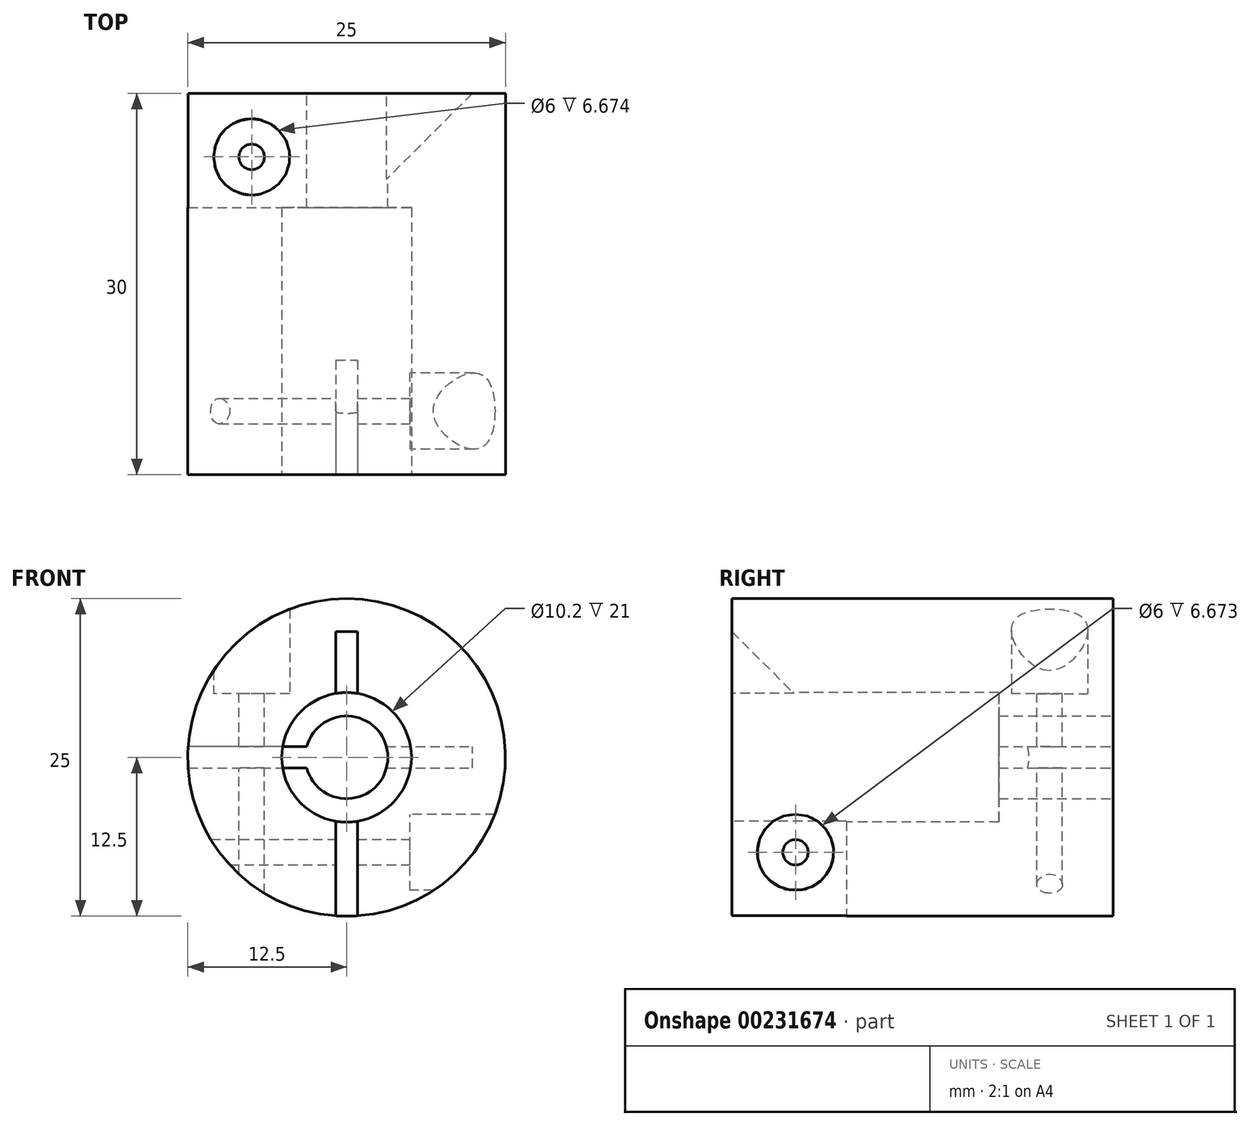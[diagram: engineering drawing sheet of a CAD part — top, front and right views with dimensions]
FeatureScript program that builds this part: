
annotation { "Feature Type Name" : "Feature", "Feature Type Description" : "" }
export const myFeature = defineFeature(function(context is Context, id is Id, definition is map)
    precondition{}
    {
        {
            var Q0;
            Q0=qCreatedBy(makeId("Front.planeOp"),FACE);
            var sketch = newSketch(context, id + "F0", { "sketchPlane" : qUnion([Q0])});
            skCircle(sketch, "E0", {"center": v(0, 0) * mm, "radius": 12.5 * mm});
            skSolve(sketch);
        }
        {
            var Q0;
            Q0 = qSketchRegion(id + "F0", true);
            extrude(context, id + "F1", {"entities" : qUnion([Q0]), "oppositeDirection" : true, "depth" : 30 * mm});
        }
        {
            var Q0;
            Q0=makeQuery(id+"F1.opExtrude","CAP_FACE",FACE,{"disambiguationData":[OSD([sQuery(id+"F0.wireOp",EDGE,"E0")])],"isStart":true});
            var sketch = newSketch(context, id + "F2", { "sketchPlane" : qUnion([Q0])});
            skCircle(sketch, "E1", {"center": v(0, 0) * mm, "radius": 5.1 * mm});
            skSolve(sketch);
        }
        {
            var Q0;
            Q0 = qSketchRegion(id + "F2", true);
            extrude(context, id + "F3", {"entities" : qUnion([Q0]), "operationType" : NewBodyOperationType.REMOVE, "oppositeDirection" : true, "depth" : 21 * mm});
        }
        {
            var Q0;
            Q0=makeQuery(id+"F1.opExtrude","CAP_FACE",FACE,{"disambiguationData":[OSD([sQuery(id+"F0.wireOp",EDGE,"E0")])],"isStart":false});
            var sketch = newSketch(context, id + "F4", { "sketchPlane" : qUnion([Q0])});
            skCircle(sketch, "E2", {"center": v(0, 0) * mm, "radius": 3.25 * mm});
            skSolve(sketch);
        }
        {
            var Q0;
            Q0 = qSketchRegion(id + "F4", true);
            extrude(context, id + "F5", {"entities" : qUnion([Q0]), "operationType" : NewBodyOperationType.REMOVE, "oppositeDirection" : true, "depth" : 30 * mm});
        }
        {
            var Q0;
            Q0=makeQuery(id+"F1.opExtrude","CAP_FACE",FACE,{"disambiguationData":[OSD([sQuery(id+"F0.wireOp",EDGE,"E0")])],"isStart":false});
            var sketch = newSketch(context, id + "F6", { "sketchPlane" : qUnion([Q0])});
            skLineSegment(sketch, "E3", {"start": v(3.14, 0.85) * mm, "end": v(12.47, 0.85) * mm});
            skLineSegment(sketch, "E4", {"start": v(12.47, -0.85) * mm, "end": v(3.14, -0.85) * mm});
            skArc(sketch, "E5", {"start": v(3.14, -0.85) * mm, "mid": v(3.25, 0) * mm, "end": v(3.14, 0.85) * mm});
            skArc(sketch, "E6", {"start": v(12.47, -0.85) * mm, "mid": v(12.5, 0) * mm, "end": v(12.47, 0.85) * mm});
            skLineSegment(sketch, "E7", {"start": v(0, 0) * mm, "end": v(12.5, 0) * mm, "construction": true});
            skLineSegment(sketch, "E8", {"start": v(0, 12.5) * mm, "end": v(0, -12.5) * mm, "construction": true});
            skSolve(sketch);
        }
        {
            var Q0;
            Q0 = qSketchRegion(id + "F6", true);
            extrude(context, id + "F7", {"entities" : qUnion([Q0]), "operationType" : NewBodyOperationType.REMOVE, "oppositeDirection" : true, "depth" : 9 * mm});
        }
        {
            var Q0;
            Q0=sQuery(id+"F6.wireOp",EDGE,"E8");
            cPlane(context, id + "F8", {"entities" : qUnion([Q0]), "cplaneType" : CPlaneType.LINE_ANGLE, "offset" : 25 * mm, "angle" : 45 * degree, "width" : 150 * mm, "height" : 150 * mm});
        }
        {
            var Q0;
            Q0=qCreatedBy(id+"F8.planeOp",FACE);
            cPlane(context, id + "F9", {"entities" : qUnion([Q0]), "cplaneType" : CPlaneType.OFFSET, "offset" : 7 * mm, "oppositeDirection" : true, "width" : 150 * mm, "height" : 150 * mm});
        }
        {
            var Q0;
            Q0=qCreatedBy(id+"F9.planeOp",FACE);
            var sketch = newSketch(context, id + "F10", { "sketchPlane" : qUnion([Q0])});
            skLineSegment(sketch, "E9", {"start": v(-18.92, 0) * mm, "end": v(-30.05, 0) * mm, "construction": true});
            skLineSegment(sketch, "E10", {"start": v(-30.03, 0.85) * mm, "end": v(-15.03, 0.85) * mm});
            skLineSegment(sketch, "E11", {"start": v(-30.03, -0.85) * mm, "end": v(-15.03, -0.85) * mm});
            skEllipticalArc(sketch, "E12.0", {});
            skPoint(sketch, "E13.orphan", {"position": v(-12.4, 0.85) * mm});
            skPoint(sketch, "E14.orphan", {"position": v(-12.4, -0.85) * mm});
            skPoint(sketch, "E15.orphan", {"position": v(-19, 0.85) * mm});
            skPoint(sketch, "E16.orphan", {"position": v(-19, -0.85) * mm});
            skLineSegment(sketch, "E17", {"start": v(-15.03, -0.85) * mm, "end": v(-15.03, 0.85) * mm});
            const initialGuessF10  = {"E12.0": [-0.021213203435596427, 0, 0, -1, 0.0125, 0.008838834764831844, 4.6443364657052575, 4.780441495064122]};
            skSetInitialGuess(sketch, initialGuessF10);
            skSolve(sketch);
        }
        {
            var Q0;
            Q0 = qSketchRegion(id + "F10", true);
            extrude(context, id + "F11", {"entities" : qUnion([Q0]), "operationType" : NewBodyOperationType.REMOVE, "endBound" : BoundingType.UP_TO_NEXT, "depth" : 25 * mm});
        }
        {
            var Q0;
            Q0=makeQuery(id+"F1.opExtrude","CAP_FACE",FACE,{"disambiguationData":[OSD([sQuery(id+"F0.wireOp",EDGE,"E0")])],"isStart":true});
            var sketch = newSketch(context, id + "F12", { "sketchPlane" : qUnion([Q0])});
            skLineSegment(sketch, "E18", {"start": v(0, 0) * mm, "end": v(0, -12.5) * mm, "construction": true});
            skArc(sketch, "E19.0", {"start": v(-0.85, -5.03) * mm, "mid": v(0, -5.1) * mm, "end": v(0.85, -5.03) * mm});
            skArc(sketch, "E20.0", {"start": v(-0.85, -12.47) * mm, "mid": v(0, -12.5) * mm, "end": v(0.85, -12.47) * mm});
            skLineSegment(sketch, "E21", {"start": v(0.85, -5.03) * mm, "end": v(0.85, -12.47) * mm});
            skLineSegment(sketch, "E22", {"start": v(-0.85, -5.03) * mm, "end": v(-0.85, -12.47) * mm});
            skLineSegment(sketch, "E23", {"start": v(12.5, 0) * mm, "end": v(-12.5, 0) * mm, "construction": true});
            skSolve(sketch);
        }
        {
            var Q0;
            Q0 = qSketchRegion(id + "F12", true);
            extrude(context, id + "F13", {"entities" : qUnion([Q0]), "operationType" : NewBodyOperationType.REMOVE, "oppositeDirection" : true, "depth" : 9 * mm});
        }
        {
            var Q0;
            Q0=sQuery(id+"F12.wireOp",EDGE,"E23");
            cPlane(context, id + "F14", {"entities" : qUnion([Q0]), "cplaneType" : CPlaneType.LINE_ANGLE, "offset" : 25 * mm, "angle" : 45 * degree, "oppositeDirection" : true, "width" : 150 * mm, "height" : 150 * mm});
        }
        {
            var Q0;
            Q0=qCreatedBy(id+"F14.planeOp",FACE);
            cPlane(context, id + "F15", {"entities" : qUnion([Q0]), "cplaneType" : CPlaneType.OFFSET, "offset" : 7 * mm, "oppositeDirection" : true, "width" : 150 * mm, "height" : 150 * mm});
        }
        {
            var Q0;
            Q0=qCreatedBy(id+"F15.planeOp",FACE);
            var sketch = newSketch(context, id + "F16", { "sketchPlane" : qUnion([Q0])});
            skLineSegment(sketch, "E24", {"start": v(0, 0) * mm, "end": v(0, 8.84) * mm, "construction": true});
            skLineSegment(sketch, "E25", {"start": v(-0.85, -6.18) * mm, "end": v(-0.85, 8.82) * mm});
            skLineSegment(sketch, "E26", {"start": v(0.85, 8.82) * mm, "end": v(0.85, -6.18) * mm});
            skEllipticalArc(sketch, "E27.0", {});
            skLineSegment(sketch, "E28", {"start": v(-0.85, -6.18) * mm, "end": v(0.85, -6.18) * mm});
            skPoint(sketch, "E29.orphan", {"position": v(-0.85, -8.82) * mm});
            skPoint(sketch, "E30.orphan", {"position": v(0.85, -8.82) * mm});
            const initialGuessF16  = {"E27.0": [0, 0, 1, 0, 0.0125, 0.008838834764831846, 1.5027438121154644, 1.6388488414743287]};
            skSetInitialGuess(sketch, initialGuessF16);
            skSolve(sketch);
        }
        {
            var Q0;
            Q0 = qSketchRegion(id + "F16", true);
            extrude(context, id + "F17", {"entities" : qUnion([Q0]), "operationType" : NewBodyOperationType.REMOVE, "depth" : 25 * mm});
        }
        {
            var Q0;
            Q0=qCreatedBy(makeId("Right.planeOp"),FACE);
            cPlane(context, id + "F18", {"entities" : qUnion([Q0]), "cplaneType" : CPlaneType.OFFSET, "offset" : 5 * mm, "width" : 150 * mm, "height" : 150 * mm});
        }
        {
            var Q0;
            Q0=qCreatedBy(id+"F18.planeOp",FACE);
            var sketch = newSketch(context, id + "F19", { "sketchPlane" : qUnion([Q0])});
            skCircle(sketch, "E31", {"center": v(5, -7.47) * mm, "radius": 3 * mm});
            skSolve(sketch);
        }
        {
            var Q0;
            Q0 = qSketchRegion(id + "F19", true);
            extrude(context, id + "F20", {"entities" : qUnion([Q0]), "operationType" : NewBodyOperationType.REMOVE, "endBound" : BoundingType.UP_TO_NEXT, "depth" : 25 * mm});
        }
        {
            var Q0;
            Q0=makeQuery(id+"F20.boolean.opBoolean","COPY",FACE,{"derivedFrom":makeQuery(id+"F20.opExtrude","CAP_FACE",FACE,{"disambiguationData":[OSD([sQuery(id+"F19.wireOp",EDGE,"E31")])],"isStart":true})});
            var sketch = newSketch(context, id + "F21", { "sketchPlane" : qUnion([Q0])});
            skCircle(sketch, "E32", {"center": v(5, -7.47) * mm, "radius": 1 * mm});
            skSolve(sketch);
        }
        {
            var Q0;
            Q0 = qSketchRegion(id + "F21", true);
            extrude(context, id + "F22", {"entities" : qUnion([Q0]), "operationType" : NewBodyOperationType.REMOVE, "endBound" : BoundingType.THROUGH_ALL, "oppositeDirection" : true, "depth" : 25 * mm});
        }
        {
            var Q0;
            Q0=qCreatedBy(makeId("Top.planeOp"),FACE);
            cPlane(context, id + "F23", {"entities" : qUnion([Q0]), "cplaneType" : CPlaneType.OFFSET, "offset" : 5 * mm, "width" : 150 * mm, "height" : 150 * mm});
        }
        {
            var Q0;
            Q0=qCreatedBy(id+"F23.planeOp",FACE);
            var sketch = newSketch(context, id + "F24", { "sketchPlane" : qUnion([Q0])});
            skCircle(sketch, "E33", {"center": v(-7.47, 25) * mm, "radius": 3 * mm});
            skSolve(sketch);
        }
        {
            var Q0;
            Q0 = qSketchRegion(id + "F24", true);
            extrude(context, id + "F25", {"entities" : qUnion([Q0]), "operationType" : NewBodyOperationType.REMOVE, "endBound" : BoundingType.UP_TO_NEXT, "depth" : 25 * mm});
        }
        {
            var Q0;
            Q0=makeQuery(id+"F25.boolean.opBoolean","COPY",FACE,{"derivedFrom":makeQuery(id+"F25.opExtrude","CAP_FACE",FACE,{"disambiguationData":[OSD([sQuery(id+"F24.wireOp",EDGE,"E33")])],"isStart":true})});
            var sketch = newSketch(context, id + "F26", { "sketchPlane" : qUnion([Q0])});
            skCircle(sketch, "E34", {"center": v(-7.47, 25) * mm, "radius": 1 * mm});
            skSolve(sketch);
        }
        {
            var Q0;
            Q0 = qSketchRegion(id + "F26", true);
            extrude(context, id + "F27", {"entities" : qUnion([Q0]), "operationType" : NewBodyOperationType.REMOVE, "endBound" : BoundingType.THROUGH_ALL, "oppositeDirection" : true, "depth" : 25 * mm});
        }
    });
